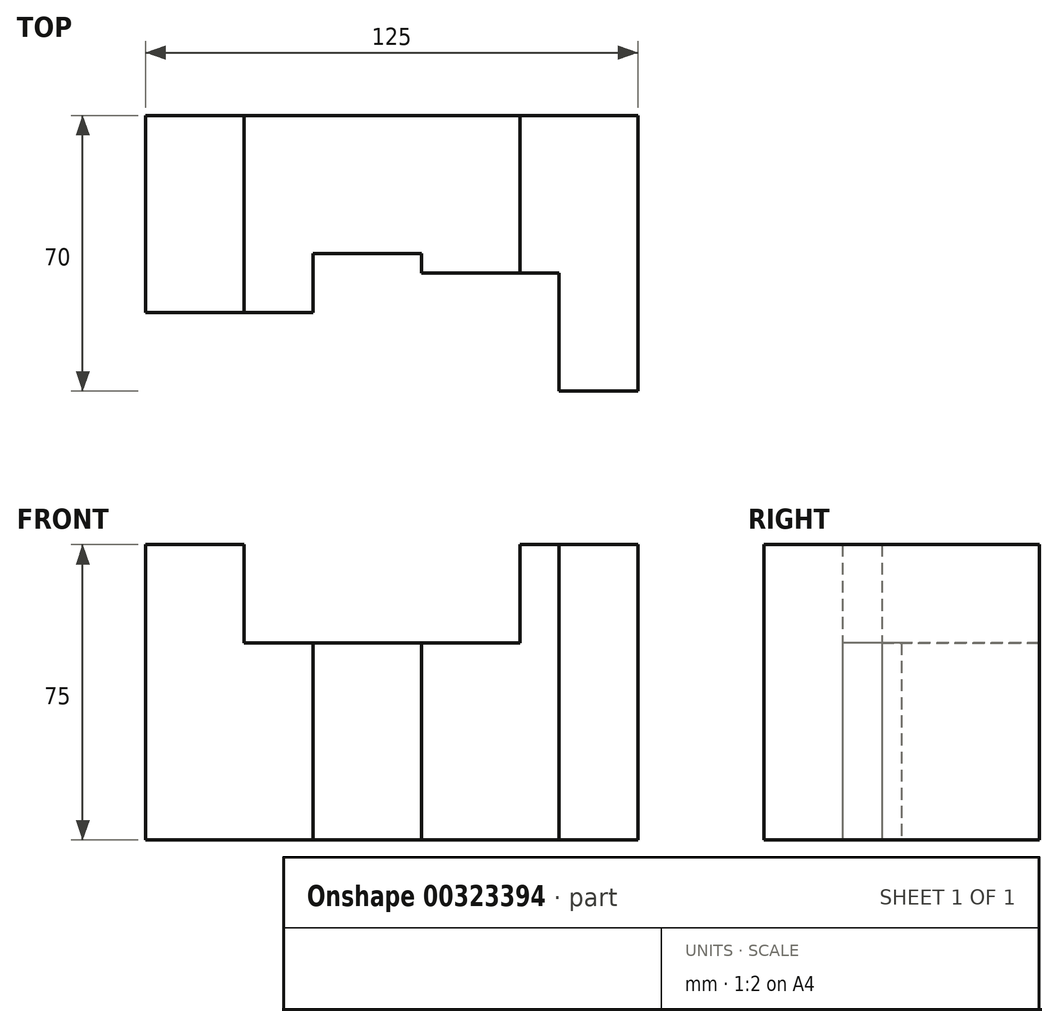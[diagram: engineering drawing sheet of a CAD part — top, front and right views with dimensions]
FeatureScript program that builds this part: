
annotation { "Feature Type Name" : "Feature", "Feature Type Description" : "" }
export const myFeature = defineFeature(function(context is Context, id is Id, definition is map)
    precondition{}
    {
        {
            var Q0;
            Q0=qCreatedBy(makeId("Top.planeOp"),FACE);
            var sketch = newSketch(context, id + "F0", { "sketchPlane" : qUnion([Q0])});
            skLineSegment(sketch, "E0", {"start": v(0, 0) * mm, "end": v(0, 50) * mm});
            skLineSegment(sketch, "E1", {"start": v(0, 50) * mm, "end": v(125, 50) * mm});
            skLineSegment(sketch, "E2", {"start": v(125, 50) * mm, "end": v(125, -20) * mm});
            skLineSegment(sketch, "E3", {"start": v(125, -20) * mm, "end": v(105, -20) * mm});
            skLineSegment(sketch, "E4", {"start": v(105, -20) * mm, "end": v(105, 0) * mm});
            skLineSegment(sketch, "E5", {"start": v(70, 15) * mm, "end": v(42.5, 15) * mm});
            skLineSegment(sketch, "E6", {"start": v(42.5, 15) * mm, "end": v(42.5, 0) * mm});
            skLineSegment(sketch, "E7", {"start": v(42.5, 0) * mm, "end": v(0, 0) * mm});
            skLineSegment(sketch, "E8", {"start": v(25, 50) * mm, "end": v(25, 0) * mm});
            skLineSegment(sketch, "E9", {"start": v(70, 15) * mm, "end": v(70, 10) * mm});
            skLineSegment(sketch, "E10", {"start": v(70, 10) * mm, "end": v(95, 10) * mm});
            skLineSegment(sketch, "E11", {"start": v(95, 10) * mm, "end": v(105, 10) * mm});
            skLineSegment(sketch, "E12", {"start": v(105, 10) * mm, "end": v(105, 0) * mm});
            skLineSegment(sketch, "E13", {"start": v(95, 10) * mm, "end": v(95, 50) * mm});
            skSolve(sketch);
        }
        {
            var Q0;
            {var subQ0=sQuery(id+"F0.wireOp",EDGE,"E0");Q0=makeQuery(id+"F0.imprint","IMPRINT",FACE,{"disambiguationData":[TD([[makeQuery(id+"F0.imprint","IMPRINT",EDGE,{"derivedFrom":subQ0}),-1.0]])]});}
            extrude(context, id + "F1", {"entities" : qUnion([Q0]), "depth" : 75 * mm});
        }
        {
            var Q0;
            Q0=makeQuery(id+"F0.imprint","IMPRINT",FACE,{"disambiguationData":[TD([[makeQuery(id+"F0.imprint","IMPRINT",EDGE,{"derivedFrom":sQuery(id+"F0.wireOp",EDGE,"E5")}),-1.0]])]});
            extrude(context, id + "F2", {"entities" : qUnion([Q0]), "operationType" : NewBodyOperationType.ADD, "depth" : 50 * mm});
        }
        {
            var Q0;
            {var subQ1=sQuery(id+"F0.wireOp",EDGE,"E2");Q0=makeQuery(id+"F0.imprint","IMPRINT",FACE,{"disambiguationData":[TD([[makeQuery(id+"F0.imprint","IMPRINT",EDGE,{"derivedFrom":subQ1}),-1.0]])]});}
            extrude(context, id + "F3", {"entities" : qUnion([Q0]), "operationType" : NewBodyOperationType.ADD, "depth" : 75 * mm});
        }
    });
